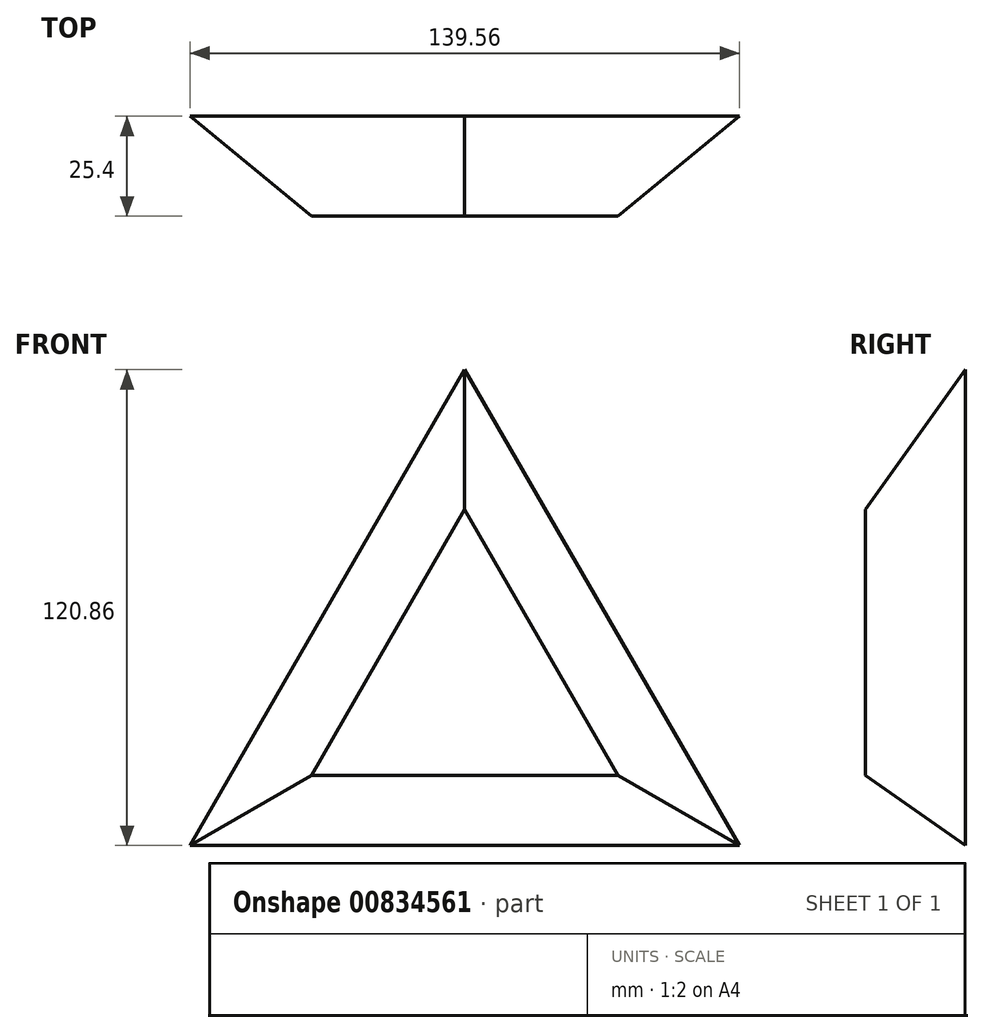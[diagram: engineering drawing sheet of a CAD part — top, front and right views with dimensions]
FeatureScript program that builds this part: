
annotation { "Feature Type Name" : "Feature", "Feature Type Description" : "" }
export const myFeature = defineFeature(function(context is Context, id is Id, definition is map)
    precondition{}
    {
        {
            var Q0;
            Q0=qCreatedBy(makeId("Front.planeOp"),FACE);
            var sketch = newSketch(context, id + "F0", { "sketchPlane" : qUnion([Q0])});
            skCircle(sketch, "E0.cCircle", {"center": v(0, 0) * mm, "radius": 40.29 * mm, "construction": true});
            skLineSegment(sketch, "E0.0", {"start": v(0, 80.57) * mm, "end": v(69.78, -40.29) * mm});
            skLineSegment(sketch, "E0.1", {"start": v(69.78, -40.29) * mm, "end": v(-69.78, -40.29) * mm});
            skLineSegment(sketch, "E0.2", {"start": v(-69.78, -40.29) * mm, "end": v(0, 80.57) * mm});
            skPoint(sketch, "E0.0.midPoint", {"position": v(34.89, 20.14) * mm});
            skSolve(sketch);
        }
        {
            var Q0;
            Q0=makeQuery(id+"F0.imprint","IMPRINT",FACE,{"disambiguationData":[TD([[makeQuery(id+"F0.imprint","IMPRINT",EDGE,{"derivedFrom":sQuery(id+"F0.wireOp",EDGE,"E0.0")}),-1.0]])]});
            extrude(context, id + "F1", {"entities" : qUnion([Q0]), "depth" : 25.4 * mm, "offsetDistance" : 25.4 * mm, "hasDraft" : true, "draftAngle" : 35 * degree, "draftPullDirection" : true});
        }
    });
